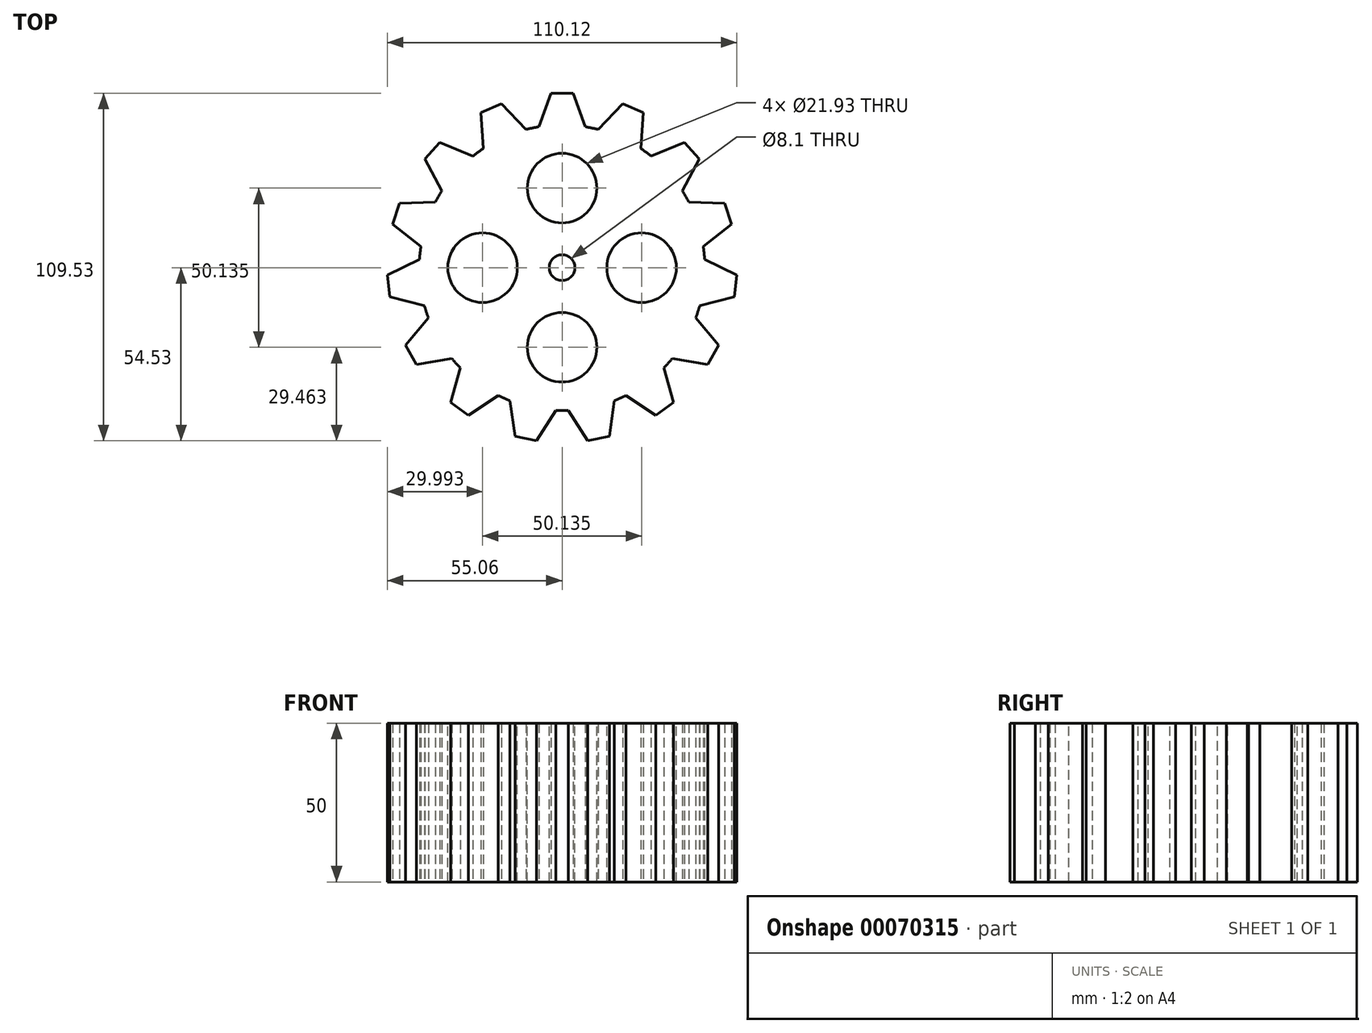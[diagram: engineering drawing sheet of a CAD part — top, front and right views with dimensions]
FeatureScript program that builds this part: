
annotation { "Feature Type Name" : "Feature", "Feature Type Description" : "" }
export const myFeature = defineFeature(function(context is Context, id is Id, definition is map)
    precondition{}
    {
        {
            var Q0;
            Q0=qCreatedBy(makeId("Top.planeOp"),FACE);
            var sketch = newSketch(context, id + "F0", { "sketchPlane" : qUnion([Q0])});
            skCircle(sketch, "E0", {"center": v(0, 0) * mm, "radius": 4.05 * mm});
            skCircle(sketch, "E1", {"center": v(0, 0) * mm, "radius": 45 * mm});
            skLineSegment(sketch, "E2", {"start": v(0, 45) * mm, "end": v(0, 55) * mm, "construction": true});
            skLineSegment(sketch, "E3", {"start": v(0, 55) * mm, "end": v(-3.5, 55) * mm});
            skLineSegment(sketch, "E4", {"start": v(-3.5, 55) * mm, "end": v(-7.36, 44.4) * mm});
            skLineSegment(sketch, "E5", {"start": v(0, 55) * mm, "end": v(-3.7, 44.85) * mm, "construction": true});
            skLineSegment(sketch, "E6.MirrorCS", {"start": v(0, 55) * mm, "end": v(3.5, 55) * mm});
            skLineSegment(sketch, "E7.MirrorCS", {"start": v(3.5, 55) * mm, "end": v(7.36, 44.4) * mm});
            skLineSegment(sketch, "E8.1.0", {"start": v(-22.37, 50.25) * mm, "end": v(-25.57, 48.82) * mm});
            skLineSegment(sketch, "E8.1.1", {"start": v(-22.37, 50.25) * mm, "end": v(-19.17, 51.67) * mm});
            skLineSegment(sketch, "E8.1.2", {"start": v(-19.17, 51.67) * mm, "end": v(-11.33, 43.55) * mm});
            skLineSegment(sketch, "E8.1.3", {"start": v(-25.57, 48.82) * mm, "end": v(-24.78, 37.56) * mm});
            skLineSegment(sketch, "E8.2.0", {"start": v(-40.87, 36.8) * mm, "end": v(-43.21, 34.2) * mm});
            skLineSegment(sketch, "E8.2.1", {"start": v(-40.87, 36.8) * mm, "end": v(-38.53, 39.4) * mm});
            skLineSegment(sketch, "E8.2.2", {"start": v(-38.53, 39.4) * mm, "end": v(-28.07, 35.18) * mm});
            skLineSegment(sketch, "E8.2.3", {"start": v(-43.21, 34.2) * mm, "end": v(-37.92, 24.24) * mm});
            skLineSegment(sketch, "E8.3.0", {"start": v(-52.3, 17) * mm, "end": v(-53.39, 13.67) * mm});
            skLineSegment(sketch, "E8.3.1", {"start": v(-52.3, 17) * mm, "end": v(-51.23, 20.32) * mm});
            skLineSegment(sketch, "E8.3.2", {"start": v(-51.23, 20.32) * mm, "end": v(-39.95, 20.72) * mm});
            skLineSegment(sketch, "E8.3.3", {"start": v(-53.39, 13.67) * mm, "end": v(-44.5, 6.72) * mm});
            skLineSegment(sketch, "E8.4.0", {"start": v(-54.7, -5.75) * mm, "end": v(-54.33, -9.23) * mm});
            skLineSegment(sketch, "E8.4.1", {"start": v(-54.7, -5.75) * mm, "end": v(-55.06, -2.27) * mm});
            skLineSegment(sketch, "E8.4.2", {"start": v(-55.06, -2.27) * mm, "end": v(-44.92, 2.68) * mm});
            skLineSegment(sketch, "E8.4.3", {"start": v(-54.33, -9.23) * mm, "end": v(-43.38, -11.96) * mm});
            skLineSegment(sketch, "E8.5.0", {"start": v(-47.63, -27.5) * mm, "end": v(-45.88, -30.53) * mm});
            skLineSegment(sketch, "E8.5.1", {"start": v(-47.63, -27.5) * mm, "end": v(-49.38, -24.47) * mm});
            skLineSegment(sketch, "E8.5.2", {"start": v(-49.38, -24.47) * mm, "end": v(-42.13, -15.82) * mm});
            skLineSegment(sketch, "E8.5.3", {"start": v(-45.88, -30.53) * mm, "end": v(-34.77, -28.57) * mm});
            skLineSegment(sketch, "E8.6.0", {"start": v(-32.33, -44.5) * mm, "end": v(-29.5, -46.55) * mm});
            skLineSegment(sketch, "E8.6.1", {"start": v(-32.33, -44.5) * mm, "end": v(-35.16, -42.44) * mm});
            skLineSegment(sketch, "E8.6.2", {"start": v(-35.16, -42.44) * mm, "end": v(-32.05, -31.59) * mm});
            skLineSegment(sketch, "E8.6.3", {"start": v(-29.5, -46.55) * mm, "end": v(-20.14, -40.24) * mm});
            skLineSegment(sketch, "E8.7.0", {"start": v(-11.44, -53.8) * mm, "end": v(-8.01, -54.53) * mm});
            skLineSegment(sketch, "E8.7.1", {"start": v(-11.44, -53.8) * mm, "end": v(-14.86, -53.07) * mm});
            skLineSegment(sketch, "E8.7.2", {"start": v(-14.86, -53.07) * mm, "end": v(-16.43, -41.9) * mm});
            skLineSegment(sketch, "E8.7.3", {"start": v(-8.01, -54.53) * mm, "end": v(-2.03, -44.95) * mm});
            skLineSegment(sketch, "E8.8.0", {"start": v(11.44, -53.8) * mm, "end": v(14.86, -53.07) * mm});
            skLineSegment(sketch, "E8.8.1", {"start": v(11.44, -53.8) * mm, "end": v(8.01, -54.53) * mm});
            skLineSegment(sketch, "E8.8.2", {"start": v(8.01, -54.53) * mm, "end": v(2.03, -44.95) * mm});
            skLineSegment(sketch, "E8.8.3", {"start": v(14.86, -53.07) * mm, "end": v(16.43, -41.9) * mm});
            skLineSegment(sketch, "E8.9.0", {"start": v(32.33, -44.5) * mm, "end": v(35.16, -42.44) * mm});
            skLineSegment(sketch, "E8.9.1", {"start": v(32.33, -44.5) * mm, "end": v(29.5, -46.55) * mm});
            skLineSegment(sketch, "E8.9.2", {"start": v(29.5, -46.55) * mm, "end": v(20.14, -40.24) * mm});
            skLineSegment(sketch, "E8.9.3", {"start": v(35.16, -42.44) * mm, "end": v(32.05, -31.59) * mm});
            skLineSegment(sketch, "E8.10.0", {"start": v(47.63, -27.5) * mm, "end": v(49.38, -24.47) * mm});
            skLineSegment(sketch, "E8.10.1", {"start": v(47.63, -27.5) * mm, "end": v(45.88, -30.53) * mm});
            skLineSegment(sketch, "E8.10.2", {"start": v(45.88, -30.53) * mm, "end": v(34.77, -28.57) * mm});
            skLineSegment(sketch, "E8.10.3", {"start": v(49.38, -24.47) * mm, "end": v(42.13, -15.82) * mm});
            skLineSegment(sketch, "E8.11.0", {"start": v(54.7, -5.75) * mm, "end": v(55.06, -2.27) * mm});
            skLineSegment(sketch, "E8.11.1", {"start": v(54.7, -5.75) * mm, "end": v(54.33, -9.23) * mm});
            skLineSegment(sketch, "E8.11.2", {"start": v(54.33, -9.23) * mm, "end": v(43.38, -11.96) * mm});
            skLineSegment(sketch, "E8.11.3", {"start": v(55.06, -2.27) * mm, "end": v(44.92, 2.68) * mm});
            skLineSegment(sketch, "E8.12.0", {"start": v(52.3, 17) * mm, "end": v(51.23, 20.32) * mm});
            skLineSegment(sketch, "E8.12.1", {"start": v(52.3, 17) * mm, "end": v(53.39, 13.67) * mm});
            skLineSegment(sketch, "E8.12.2", {"start": v(53.39, 13.67) * mm, "end": v(44.5, 6.72) * mm});
            skLineSegment(sketch, "E8.12.3", {"start": v(51.23, 20.32) * mm, "end": v(39.95, 20.72) * mm});
            skLineSegment(sketch, "E8.13.0", {"start": v(40.87, 36.8) * mm, "end": v(38.53, 39.4) * mm});
            skLineSegment(sketch, "E8.13.1", {"start": v(40.87, 36.8) * mm, "end": v(43.21, 34.2) * mm});
            skLineSegment(sketch, "E8.13.2", {"start": v(43.21, 34.2) * mm, "end": v(37.92, 24.24) * mm});
            skLineSegment(sketch, "E8.13.3", {"start": v(38.53, 39.4) * mm, "end": v(28.07, 35.18) * mm});
            skLineSegment(sketch, "E8.14.0", {"start": v(22.37, 50.25) * mm, "end": v(19.17, 51.67) * mm});
            skLineSegment(sketch, "E8.14.1", {"start": v(22.37, 50.25) * mm, "end": v(25.57, 48.82) * mm});
            skLineSegment(sketch, "E8.14.2", {"start": v(25.57, 48.82) * mm, "end": v(24.78, 37.56) * mm});
            skLineSegment(sketch, "E8.14.3", {"start": v(19.17, 51.67) * mm, "end": v(11.33, 43.55) * mm});
            skSolve(sketch);
        }
        {
            var Q0;
            Q0=makeQuery(id+"F0.imprint","IMPRINT",FACE,{"disambiguationData":[TD([[makeQuery(id+"F0.imprint","IMPRINT",EDGE,{"derivedFrom":sQuery(id+"F0.wireOp",EDGE,"E8.8.0")}),1.0]])]});
            var Q1;
            Q1=makeQuery(id+"F0.imprint","IMPRINT",FACE,{"disambiguationData":[TD([[makeQuery(id+"F0.imprint","IMPRINT",EDGE,{"derivedFrom":sQuery(id+"F0.wireOp",EDGE,"E8.7.0")}),1.0]])]});
            var Q2;
            Q2=makeQuery(id+"F0.imprint","IMPRINT",FACE,{"disambiguationData":[TD([[makeQuery(id+"F0.imprint","IMPRINT",EDGE,{"derivedFrom":sQuery(id+"F0.wireOp",EDGE,"E8.6.0")}),1.0]])]});
            var Q3;
            Q3=makeQuery(id+"F0.imprint","IMPRINT",FACE,{"disambiguationData":[TD([[makeQuery(id+"F0.imprint","IMPRINT",EDGE,{"derivedFrom":sQuery(id+"F0.wireOp",EDGE,"E8.5.0")}),1.0]])]});
            var Q4;
            Q4=makeQuery(id+"F0.imprint","IMPRINT",FACE,{"disambiguationData":[TD([[makeQuery(id+"F0.imprint","IMPRINT",EDGE,{"derivedFrom":sQuery(id+"F0.wireOp",EDGE,"E8.4.0")}),1.0]])]});
            var Q5;
            Q5=makeQuery(id+"F0.imprint","IMPRINT",FACE,{"disambiguationData":[TD([[makeQuery(id+"F0.imprint","IMPRINT",EDGE,{"derivedFrom":sQuery(id+"F0.wireOp",EDGE,"E8.2.0")}),1.0]])]});
            var Q6;
            Q6=makeQuery(id+"F0.imprint","IMPRINT",FACE,{"disambiguationData":[TD([[makeQuery(id+"F0.imprint","IMPRINT",EDGE,{"derivedFrom":sQuery(id+"F0.wireOp",EDGE,"E8.3.0")}),1.0]])]});
            var Q7;
            Q7=makeQuery(id+"F0.imprint","IMPRINT",FACE,{"disambiguationData":[TD([[makeQuery(id+"F0.imprint","IMPRINT",EDGE,{"derivedFrom":sQuery(id+"F0.wireOp",EDGE,"E8.1.0")}),1.0]])]});
            var Q8;
            Q8=makeQuery(id+"F0.imprint","IMPRINT",FACE,{"disambiguationData":[TD([[makeQuery(id+"F0.imprint","IMPRINT",EDGE,{"derivedFrom":sQuery(id+"F0.wireOp",EDGE,"E3")}),1.0]])]});
            var Q9;
            Q9=makeQuery(id+"F0.imprint","IMPRINT",FACE,{"disambiguationData":[TD([[makeQuery(id+"F0.imprint","IMPRINT",EDGE,{"derivedFrom":sQuery(id+"F0.wireOp",EDGE,"E8.14.0")}),1.0]])]});
            var Q10;
            Q10=makeQuery(id+"F0.imprint","IMPRINT",FACE,{"disambiguationData":[TD([[makeQuery(id+"F0.imprint","IMPRINT",EDGE,{"derivedFrom":sQuery(id+"F0.wireOp",EDGE,"E8.13.0")}),1.0]])]});
            var Q11;
            Q11=makeQuery(id+"F0.imprint","IMPRINT",FACE,{"disambiguationData":[TD([[makeQuery(id+"F0.imprint","IMPRINT",EDGE,{"derivedFrom":sQuery(id+"F0.wireOp",EDGE,"E8.12.0")}),1.0]])]});
            var Q12;
            Q12=makeQuery(id+"F0.imprint","IMPRINT",FACE,{"disambiguationData":[TD([[makeQuery(id+"F0.imprint","IMPRINT",EDGE,{"derivedFrom":sQuery(id+"F0.wireOp",EDGE,"E8.10.0")}),1.0]])]});
            var Q13;
            Q13=makeQuery(id+"F0.imprint","IMPRINT",FACE,{"disambiguationData":[TD([[makeQuery(id+"F0.imprint","IMPRINT",EDGE,{"derivedFrom":sQuery(id+"F0.wireOp",EDGE,"E0")}),-1.0]])]});
            var Q14;
            Q14=makeQuery(id+"F0.imprint","IMPRINT",FACE,{"disambiguationData":[TD([[makeQuery(id+"F0.imprint","IMPRINT",EDGE,{"derivedFrom":sQuery(id+"F0.wireOp",EDGE,"E8.9.0")}),1.0]])]});
            var Q15;
            Q15=makeQuery(id+"F0.imprint","IMPRINT",FACE,{"disambiguationData":[TD([[makeQuery(id+"F0.imprint","IMPRINT",EDGE,{"derivedFrom":sQuery(id+"F0.wireOp",EDGE,"E8.11.0")}),1.0]])]});
            var Q16;
            Q16=makeQuery(id+"F0.imprint","IMPRINT",FACE,{"disambiguationData":[TD([[makeQuery(id+"F0.imprint","IMPRINT",EDGE,{"derivedFrom":sQuery(id+"F0.wireOp",EDGE,"E0")}),1.0]])]});
            extrude(context, id + "F1", {"entities" : qUnion([Q0, Q1, Q2, Q3, Q4, Q5, Q6, Q7, Q8, Q9, Q10, Q11, Q12, Q13, Q14, Q15, Q16]), "depth" : 50 * mm});
        }
        {
            var Q0;
            Q0=makeQuery(id+"F1.opExtrude","CAP_FACE",FACE,{"disambiguationData":[OSD([sQuery(id+"F0.wireOp",EDGE,"E1"),sQuery(id+"F0.wireOp",EDGE,"E3"),sQuery(id+"F0.wireOp",EDGE,"E4"),sQuery(id+"F0.wireOp",EDGE,"E6.MirrorCS"),sQuery(id+"F0.wireOp",EDGE,"E7.MirrorCS"),sQuery(id+"F0.wireOp",EDGE,"E8.1.0"),sQuery(id+"F0.wireOp",EDGE,"E8.1.1"),sQuery(id+"F0.wireOp",EDGE,"E8.1.2"),sQuery(id+"F0.wireOp",EDGE,"E8.1.3"),sQuery(id+"F0.wireOp",EDGE,"E8.2.0"),sQuery(id+"F0.wireOp",EDGE,"E8.2.1"),sQuery(id+"F0.wireOp",EDGE,"E8.2.2"),sQuery(id+"F0.wireOp",EDGE,"E8.2.3"),sQuery(id+"F0.wireOp",EDGE,"E8.3.0"),sQuery(id+"F0.wireOp",EDGE,"E8.3.1"),sQuery(id+"F0.wireOp",EDGE,"E8.3.2"),sQuery(id+"F0.wireOp",EDGE,"E8.3.3"),sQuery(id+"F0.wireOp",EDGE,"E8.4.0"),sQuery(id+"F0.wireOp",EDGE,"E8.4.1"),sQuery(id+"F0.wireOp",EDGE,"E8.4.2"),sQuery(id+"F0.wireOp",EDGE,"E8.4.3"),sQuery(id+"F0.wireOp",EDGE,"E8.5.0"),sQuery(id+"F0.wireOp",EDGE,"E8.5.1"),sQuery(id+"F0.wireOp",EDGE,"E8.5.2"),sQuery(id+"F0.wireOp",EDGE,"E8.5.3"),sQuery(id+"F0.wireOp",EDGE,"E8.6.0"),sQuery(id+"F0.wireOp",EDGE,"E8.6.1"),sQuery(id+"F0.wireOp",EDGE,"E8.6.2"),sQuery(id+"F0.wireOp",EDGE,"E8.6.3"),sQuery(id+"F0.wireOp",EDGE,"E8.7.0"),sQuery(id+"F0.wireOp",EDGE,"E8.7.1"),sQuery(id+"F0.wireOp",EDGE,"E8.7.2"),sQuery(id+"F0.wireOp",EDGE,"E8.7.3"),sQuery(id+"F0.wireOp",EDGE,"E8.8.0"),sQuery(id+"F0.wireOp",EDGE,"E8.8.1"),sQuery(id+"F0.wireOp",EDGE,"E8.8.2"),sQuery(id+"F0.wireOp",EDGE,"E8.8.3"),sQuery(id+"F0.wireOp",EDGE,"E8.9.0"),sQuery(id+"F0.wireOp",EDGE,"E8.9.1"),sQuery(id+"F0.wireOp",EDGE,"E8.9.2"),sQuery(id+"F0.wireOp",EDGE,"E8.9.3"),sQuery(id+"F0.wireOp",EDGE,"E8.10.0"),sQuery(id+"F0.wireOp",EDGE,"E8.10.1"),sQuery(id+"F0.wireOp",EDGE,"E8.10.2"),sQuery(id+"F0.wireOp",EDGE,"E8.10.3"),sQuery(id+"F0.wireOp",EDGE,"E8.11.0"),sQuery(id+"F0.wireOp",EDGE,"E8.11.1"),sQuery(id+"F0.wireOp",EDGE,"E8.11.2"),sQuery(id+"F0.wireOp",EDGE,"E8.11.3"),sQuery(id+"F0.wireOp",EDGE,"E8.12.0"),sQuery(id+"F0.wireOp",EDGE,"E8.12.1"),sQuery(id+"F0.wireOp",EDGE,"E8.12.2"),sQuery(id+"F0.wireOp",EDGE,"E8.12.3"),sQuery(id+"F0.wireOp",EDGE,"E8.13.0"),sQuery(id+"F0.wireOp",EDGE,"E8.13.1"),sQuery(id+"F0.wireOp",EDGE,"E8.13.2"),sQuery(id+"F0.wireOp",EDGE,"E8.13.3"),sQuery(id+"F0.wireOp",EDGE,"E8.14.0"),sQuery(id+"F0.wireOp",EDGE,"E8.14.1"),sQuery(id+"F0.wireOp",EDGE,"E8.14.2"),sQuery(id+"F0.wireOp",EDGE,"E8.14.3")])],"isStart":false});
            var sketch = newSketch(context, id + "F2", { "sketchPlane" : qUnion([Q0])});
            skCircle(sketch, "E9", {"center": v(0, 0) * mm, "radius": 4.05 * mm});
            skCircle(sketch, "E10", {"center": v(0, 25.07) * mm, "radius": 10.96 * mm});
            skCircle(sketch, "E11.1.0", {"center": v(-25.07, 0) * mm, "radius": 10.96 * mm});
            skCircle(sketch, "E11.2.0", {"center": v(0, -25.07) * mm, "radius": 10.96 * mm});
            skCircle(sketch, "E11.3.0", {"center": v(25.07, 0) * mm, "radius": 10.96 * mm});
            skSolve(sketch);
        }
        {
            var Q0;
            Q0=makeQuery(id+"F2.imprint","IMPRINT",FACE,{"disambiguationData":[TD([[makeQuery(id+"F2.imprint","IMPRINT",EDGE,{"derivedFrom":sQuery(id+"F2.wireOp",EDGE,"E10")}),1.0]])]});
            var Q1;
            Q1=makeQuery(id+"F2.imprint","IMPRINT",FACE,{"disambiguationData":[TD([[makeQuery(id+"F2.imprint","IMPRINT",EDGE,{"derivedFrom":sQuery(id+"F2.wireOp",EDGE,"E11.1.0")}),1.0]])]});
            var Q2;
            Q2=makeQuery(id+"F2.imprint","IMPRINT",FACE,{"disambiguationData":[TD([[makeQuery(id+"F2.imprint","IMPRINT",EDGE,{"derivedFrom":sQuery(id+"F2.wireOp",EDGE,"E11.3.0")}),1.0]])]});
            var Q3;
            Q3=makeQuery(id+"F2.imprint","IMPRINT",FACE,{"disambiguationData":[TD([[makeQuery(id+"F2.imprint","IMPRINT",EDGE,{"derivedFrom":sQuery(id+"F2.wireOp",EDGE,"E9")}),1.0]])]});
            var Q4;
            Q4=makeQuery(id+"F2.imprint","IMPRINT",FACE,{"disambiguationData":[TD([[makeQuery(id+"F2.imprint","IMPRINT",EDGE,{"derivedFrom":sQuery(id+"F2.wireOp",EDGE,"E11.2.0")}),1.0]])]});
            extrude(context, id + "F3", {"entities" : qUnion([Q0, Q1, Q2, Q3, Q4]), "operationType" : NewBodyOperationType.REMOVE, "oppositeDirection" : true, "depth" : 100 * mm});
        }
    });
